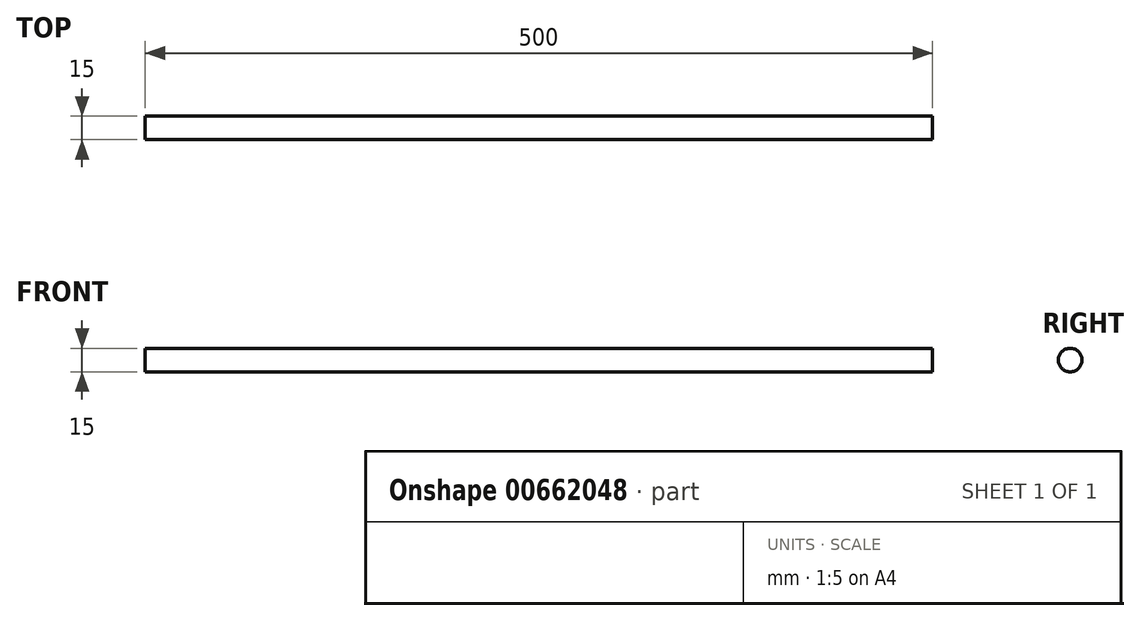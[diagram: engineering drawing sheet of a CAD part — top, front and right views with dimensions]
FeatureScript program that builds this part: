
annotation { "Feature Type Name" : "Feature", "Feature Type Description" : "" }
export const myFeature = defineFeature(function(context is Context, id is Id, definition is map)
    precondition{}
    {
        {
            var Q0;
            Q0=qCreatedBy(makeId("Front.planeOp"),FACE);
            var sketch = newSketch(context, id + "F0", { "sketchPlane" : qUnion([Q0])});
            skLineSegment(sketch, "E0.bottom", {"start": v(-94.74, 7.5) * mm, "end": v(405.26, 7.5) * mm});
            skLineSegment(sketch, "E0.top", {"start": v(-94.74, 0) * mm, "end": v(405.26, 0) * mm});
            skLineSegment(sketch, "E0.left", {"start": v(-94.74, 7.5) * mm, "end": v(-94.74, 0) * mm});
            skLineSegment(sketch, "E0.right", {"start": v(405.26, 7.5) * mm, "end": v(405.26, 0) * mm});
            skSolve(sketch);
        }
        {
            var Q0;
            Q0=makeQuery(id+"F0.imprint","IMPRINT",FACE,{"disambiguationData":[TD([[makeQuery(id+"F0.imprint","IMPRINT",EDGE,{"derivedFrom":sQuery(id+"F0.wireOp",EDGE,"E0.bottom")}),-1.0]])]});
            var Q1;
            Q1=sQuery(id+"F0.wireOp",EDGE,"E0.top");
            revolve(context, id + "F1", {"entities" : qUnion([Q0]), "axis" : qUnion([Q1]), "revolveType" : RevolveType.FULL});
        }
    });
